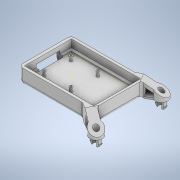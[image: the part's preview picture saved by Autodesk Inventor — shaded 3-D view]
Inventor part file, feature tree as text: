
AUTODESK INVENTOR PART (.ipt)
format: ipt  version: 2020 (Build 240168000, 168)  size: 397,312 bytes
history: native  units: in
note: dims shown in document units (in); Inventor stores cm internally (conversion verified against a paired STEP export)
features: extrude x13, sketch x12, mirror x3, chamfer x3, fillet x2, shell x1
ambient origin geometry x8: Origin, YZ Plane, XZ Plane, XY Plane, X Axis, Y Axis, Z Axis, Center Point
bodies: Solid1 (feature_tree)
feature tree (34):
  extrude  "Extrusion1"  Depth=0.4in
  shell  "Shell1"  Thickness=1.0in
  fillet  "Fillet1"  Radius=0.4in
  extrude  "Extrusion2"  Depth=0.25in
  sketch  "Sketch3"  dims[d8=0.125in d9=0.5in d10=0.0in]
  extrude  "Extrusion3"  Depth=0.5in TaperAngle=0.0deg
  extrude  "Extrusion4"  Depth=0.2in
  extrude  "Extrusion5"  Depth=0.1in
  fillet  "Fillet2"  Radius=0.1in
  extrude  "Extrusion6"  Depth=0.4in TaperAngle=0.0deg
  mirror  "Mirror1"
  extrude  "Extrusion7"  Depth=1.6in
  mirror  "Mirror2"
  chamfer  "Chamfer1"  Distance=0.1969in
  extrude  "Extrusion8"  Depth=0.0984in
  extrude  "Extrusion9"  Depth=0.0984in TaperAngle=0.0deg
  chamfer  "Chamfer2"  Distance=1.5812in
  chamfer  "Chamfer3"  Distance=0.1969in Angle=45.0deg
  extrude  "Extrusion10"  Depth=0.0984in
  extrude  "Extrusion11"  Depth=0.0984in
  mirror  "Mirror3"
  extrude  "Extrusion13"  Depth=0.3937in TaperAngle=0.0deg
  extrude  "Extrusion14"  Depth=0.0984in
  sketch  "Sketch1"  dims[d0=3.5in d1=5.0in d3=1.0in d4=0.0in d5=0.4in]
  sketch  "Sketch2"  dims[d6=0.25in d7=3.15in]
  sketch  "Sketch5"  dims[d11=1.8in d12=0.2in]
  sketch  "Sketch6"  dims[d13=0.3in d14=0.0in d15=4.65in d16=0.1in]
  sketch  "Sketch8"  dims[d20=0.25in d21=0.0in d22=0.4in d23=0.0in]
  sketch  "Sketch9"  dims[d24=0.25in d25=1.6in]
  sketch  "Sketch10"  dims[d26=0.7in]
  sketch  "Sketch11"  dims[d27=30.0deg]
  sketch  "Sketch12"  dims[d28=0.3in]
  sketch  "Sketch14"  dims[d29=1.9358in]
  sketch  "Sketch15"  dims[d30=0.5906in d31=0.1969in d32=0.1969in d33=0.7874in d34=0.0in d35=1.5812in d36=0.0in d37=0.1969in d38=0.0492in d39=45.0deg d40=0.5512in d41=0.0984in d42=0.3937in d43=0.0in d44=0.6496in d45=0.1575in d46=0.0in d47=0.0984in d48=0.1575in d49=45.0deg d50=0.0984in d51=0.1575in d52=45.0deg d53=3.937in d54=0.0in d55=1.0812in d56=0.0in d59=0.2362in d60=0.2362in d61=0.1969in d62=0.1969in d63=0.1969in d64=0.1969in d65=0.4562in d66=0.0in d67=0.4921in d68=0.0984in d69=0.0in]
